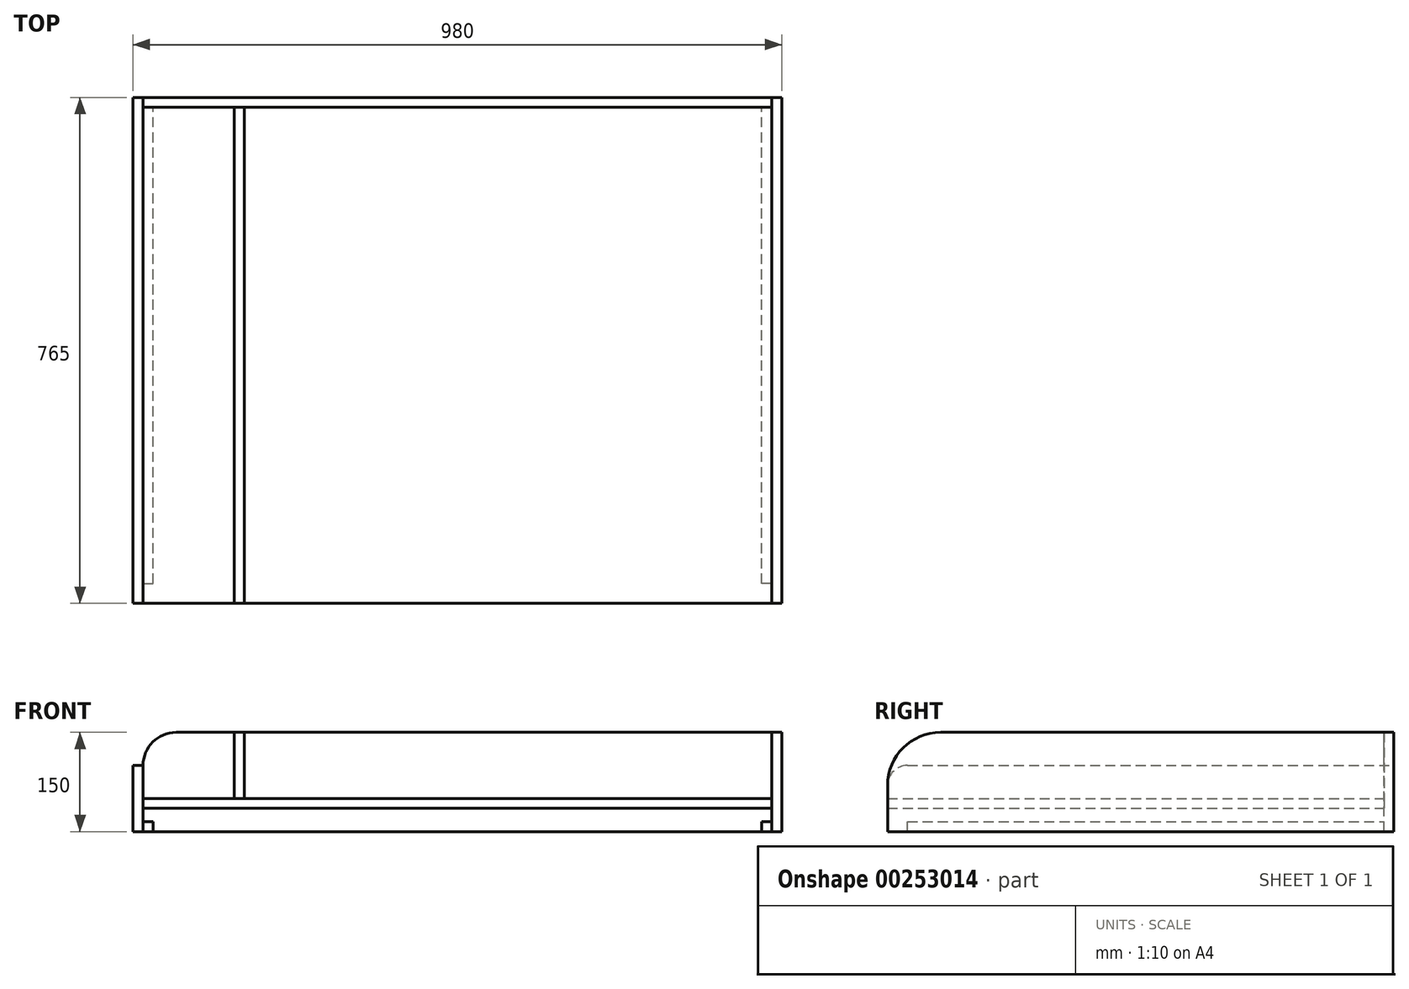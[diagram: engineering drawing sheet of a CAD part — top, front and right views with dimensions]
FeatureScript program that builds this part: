
annotation { "Feature Type Name" : "Feature", "Feature Type Description" : "" }
export const myFeature = defineFeature(function(context is Context, id is Id, definition is map)
    precondition{}
    {
        {
            var Q0;
            Q0=qCreatedBy(makeId("Top.planeOp"),FACE);
            var sketch = newSketch(context, id + "F0", { "sketchPlane" : qUnion([Q0])});
            skLineSegment(sketch, "E0.bottom", {"start": v(0, 0) * mm, "end": v(950, 0) * mm});
            skLineSegment(sketch, "E0.top", {"start": v(0, 750) * mm, "end": v(950, 750) * mm});
            skLineSegment(sketch, "E0.left", {"start": v(0, 0) * mm, "end": v(0, 750) * mm});
            skLineSegment(sketch, "E0.right", {"start": v(950, 0) * mm, "end": v(950, 750) * mm});
            skSolve(sketch);
        }
        {
            var Q0;
            Q0 = qSketchRegion(id + "F0", true);
            extrude(context, id + "F1", {"entities" : qUnion([Q0]), "depth" : 15 * mm});
        }
        {
            var Q0;
            Q0=makeQuery(id+"F1.opExtrude","SWEPT_FACE",FACE,{"disambiguationData":[OSD([sQuery(id+"F0.wireOp",EDGE,"E0.right")])]});
            var sketch = newSketch(context, id + "F2", { "sketchPlane" : qUnion([Q0])});
            skLineSegment(sketch, "E1.bottom", {"start": v(0, -35) * mm, "end": v(765, -35) * mm});
            skLineSegment(sketch, "E1.top", {"start": v(0, 115) * mm, "end": v(765, 115) * mm});
            skLineSegment(sketch, "E1.left", {"start": v(0, -35) * mm, "end": v(0, 115) * mm});
            skLineSegment(sketch, "E1.right", {"start": v(765, -35) * mm, "end": v(765, 115) * mm});
            skSolve(sketch);
        }
        {
            var Q0;
            {var subQ5=sQuery(id+"F2.wireOp",EDGE,"E1.bottom");Q0=makeQuery(id+"F2.imprint","IMPRINT",FACE,{"disambiguationData":[TD([[makeQuery(id+"F2.imprint","IMPRINT",EDGE,{"derivedFrom":subQ5}),1.0]])]});}
            var Q1;
            {var subQ1=sQuery(id+"F0.wireOp",EDGE,"E0.right");var subQ2=makeQuery(id+"F1.opExtrude","CAP_EDGE",EDGE,{"disambiguationData":[OSD([subQ1])],"isStart":true});Q1=makeQuery(id+"F2.imprint","IMPRINT",FACE,{"disambiguationData":[TD([[makeQuery(id+"F2.imprint","IMPRINT",EDGE,{"derivedFrom":subQ2}),1.0]])]});}
            extrude(context, id + "F3", {"entities" : qUnion([Q0, Q1]), "depth" : 15 * mm});
        }
        {
            var Q0;
            Q0=makeQuery(id+"F3.opExtrude","SWEPT_EDGE",EDGE,{"disambiguationData":[OSD([sQuery(id+"F2.wireOp",EDGE,"tLncR51a-jdyt-qLsX-Fpy9-QJLA5nKiiK64.top"),sQuery(id+"F2.wireOp",EDGE,"tLncR51a-jdyt-qLsX-Fpy9-QJLA5nKiiK64.left")])]});
            var Q1;
            Q1=makeQuery(id+"F3.opExtrude","SWEPT_EDGE",EDGE,{"disambiguationData":[OSD([sQuery(id+"F2.wireOp",EDGE,"E1.top"),sQuery(id+"F2.wireOp",EDGE,"E1.left")])]});
            fillet(context, id + "F4", {"entities" : qUnion([Q0, Q1]), "radius" : 80 * mm, "tangentPropagation" : true, "allowEdgeOverflow" : false});
        }
        {
            var Q0;
            Q0=makeQuery(id+"F1.opExtrude","SWEPT_FACE",FACE,{"disambiguationData":[OSD([sQuery(id+"F0.wireOp",EDGE,"E0.left")])]});
            var sketch = newSketch(context, id + "F5", { "sketchPlane" : qUnion([Q0])});
            skLineSegment(sketch, "E2.bottom", {"start": v(0, -35) * mm, "end": v(-765, -35) * mm});
            skLineSegment(sketch, "E2.top", {"start": v(0, 65) * mm, "end": v(-765, 65) * mm});
            skLineSegment(sketch, "E2.left", {"start": v(0, -35) * mm, "end": v(0, 65) * mm});
            skLineSegment(sketch, "E2.right", {"start": v(-765, -35) * mm, "end": v(-765, 65) * mm});
            skSolve(sketch);
        }
        {
            var Q0;
            Q0 = qSketchRegion(id + "F5", true);
            extrude(context, id + "F6", {"entities" : qUnion([Q0]), "depth" : 15 * mm});
        }
        {
            var Q0;
            Q0=makeQuery(id+"F6.opExtrude","SWEPT_EDGE",EDGE,{"disambiguationData":[OSD([sQuery(id+"F5.wireOp",EDGE,"E2.top"),sQuery(id+"F5.wireOp",EDGE,"E2.left")])]});
            fillet(context, id + "F7", {"entities" : qUnion([Q0]), "radius" : 30 * mm, "tangentPropagation" : true, "allowEdgeOverflow" : false});
        }
        {
            var Q0;
            Q0=makeQuery(id+"F1.opExtrude","CAP_FACE",FACE,{"disambiguationData":[OSD([sQuery(id+"F0.wireOp",EDGE,"E0.bottom"),sQuery(id+"F0.wireOp",EDGE,"E0.top"),sQuery(id+"F0.wireOp",EDGE,"E0.left"),sQuery(id+"F0.wireOp",EDGE,"E0.right")])],"isStart":false});
            var sketch = newSketch(context, id + "F8", { "sketchPlane" : qUnion([Q0])});
            skLineSegment(sketch, "E3.bottom", {"start": v(153, 0) * mm, "end": v(138, 0) * mm});
            skLineSegment(sketch, "E3.top", {"start": v(153, 750) * mm, "end": v(138, 750) * mm});
            skLineSegment(sketch, "E3.left", {"start": v(153, 0) * mm, "end": v(153, 750) * mm});
            skLineSegment(sketch, "E3.right", {"start": v(138, 0) * mm, "end": v(138, 750) * mm});
            skSolve(sketch);
        }
        {
            var Q0;
            Q0 = qSketchRegion(id + "F8", true);
            extrude(context, id + "F9", {"entities" : qUnion([Q0]), "depth" : 100 * mm});
        }
        {
            var Q0;
            Q0=makeQuery(id+"F9.opExtrude","CAP_EDGE",EDGE,{"disambiguationData":[OSD([sQuery(id+"F8.wireOp",EDGE,"E3.bottom")])],"isStart":false});
            fillet(context, id + "F10", {"entities" : qUnion([Q0]), "radius" : 80 * mm, "tangentPropagation" : true, "allowEdgeOverflow" : false});
        }
        {
            var Q0;
            Q0=makeQuery(id+"F1.opExtrude","SWEPT_FACE",FACE,{"disambiguationData":[OSD([sQuery(id+"F0.wireOp",EDGE,"E0.top")])]});
            var sketch = newSketch(context, id + "F11", { "sketchPlane" : qUnion([Q0])});
            skLineSegment(sketch, "E4.bottom", {"start": v(-950, -35) * mm, "end": v(0, -35) * mm});
            skLineSegment(sketch, "E4.top", {"start": v(-950, 115) * mm, "end": v(0, 115) * mm});
            skLineSegment(sketch, "E4.left", {"start": v(-950, -35) * mm, "end": v(-950, 115) * mm});
            skLineSegment(sketch, "E4.right", {"start": v(0, -35) * mm, "end": v(0, 115) * mm});
            skSolve(sketch);
        }
        {
            var Q0;
            Q0 = qSketchRegion(id + "F11", true);
            extrude(context, id + "F12", {"entities" : qUnion([Q0]), "depth" : 15 * mm});
        }
        {
            var Q0;
            Q0=makeQuery(id+"F12.opExtrude","SWEPT_EDGE",EDGE,{"disambiguationData":[OSD([sQuery(id+"F11.wireOp",EDGE,"hnQzqrfe-OLvb-vpgu-pYrF-JI92xdY31qPS.top"),sQuery(id+"F11.wireOp",EDGE,"hnQzqrfe-OLvb-vpgu-pYrF-JI92xdY31qPS.left")])]});
            var Q1;
            Q1=makeQuery(id+"F12.opExtrude","SWEPT_EDGE",EDGE,{"disambiguationData":[OSD([sQuery(id+"F11.wireOp",EDGE,"E4.top"),sQuery(id+"F11.wireOp",EDGE,"E4.right")])]});
            fillet(context, id + "F13", {"entities" : qUnion([Q0, Q1]), "radius" : 50 * mm, "tangentPropagation" : true, "allowEdgeOverflow" : false});
        }
        {
            var Q0;
            Q0=makeQuery(id+"F12.opExtrude","CAP_FACE",FACE,{"disambiguationData":[OSD([sQuery(id+"F11.wireOp",EDGE,"E4.bottom"),sQuery(id+"F11.wireOp",EDGE,"E4.top"),sQuery(id+"F11.wireOp",EDGE,"E4.left"),sQuery(id+"F11.wireOp",EDGE,"E4.right")])],"isStart":true});
            var sketch = newSketch(context, id + "F14", { "sketchPlane" : qUnion([Q0])});
            skLineSegment(sketch, "E5.bottom", {"start": v(0, -35) * mm, "end": v(15, -35) * mm});
            skLineSegment(sketch, "E5.top", {"start": v(0, -20) * mm, "end": v(15, -20) * mm});
            skLineSegment(sketch, "E5.left", {"start": v(0, -35) * mm, "end": v(0, -20) * mm});
            skLineSegment(sketch, "E5.right", {"start": v(15, -35) * mm, "end": v(15, -20) * mm});
            skLineSegment(sketch, "E6.bottom", {"start": v(950, -35) * mm, "end": v(935, -35) * mm});
            skLineSegment(sketch, "E6.top", {"start": v(950, -20) * mm, "end": v(935, -20) * mm});
            skLineSegment(sketch, "E6.left", {"start": v(950, -35) * mm, "end": v(950, -20) * mm});
            skLineSegment(sketch, "E6.right", {"start": v(935, -35) * mm, "end": v(935, -20) * mm});
            skSolve(sketch);
        }
        {
            var Q0;
            Q0 = qSketchRegion(id + "F14", true);
            extrude(context, id + "F15", {"entities" : qUnion([Q0]), "depth" : 720 * mm});
        }
    });
